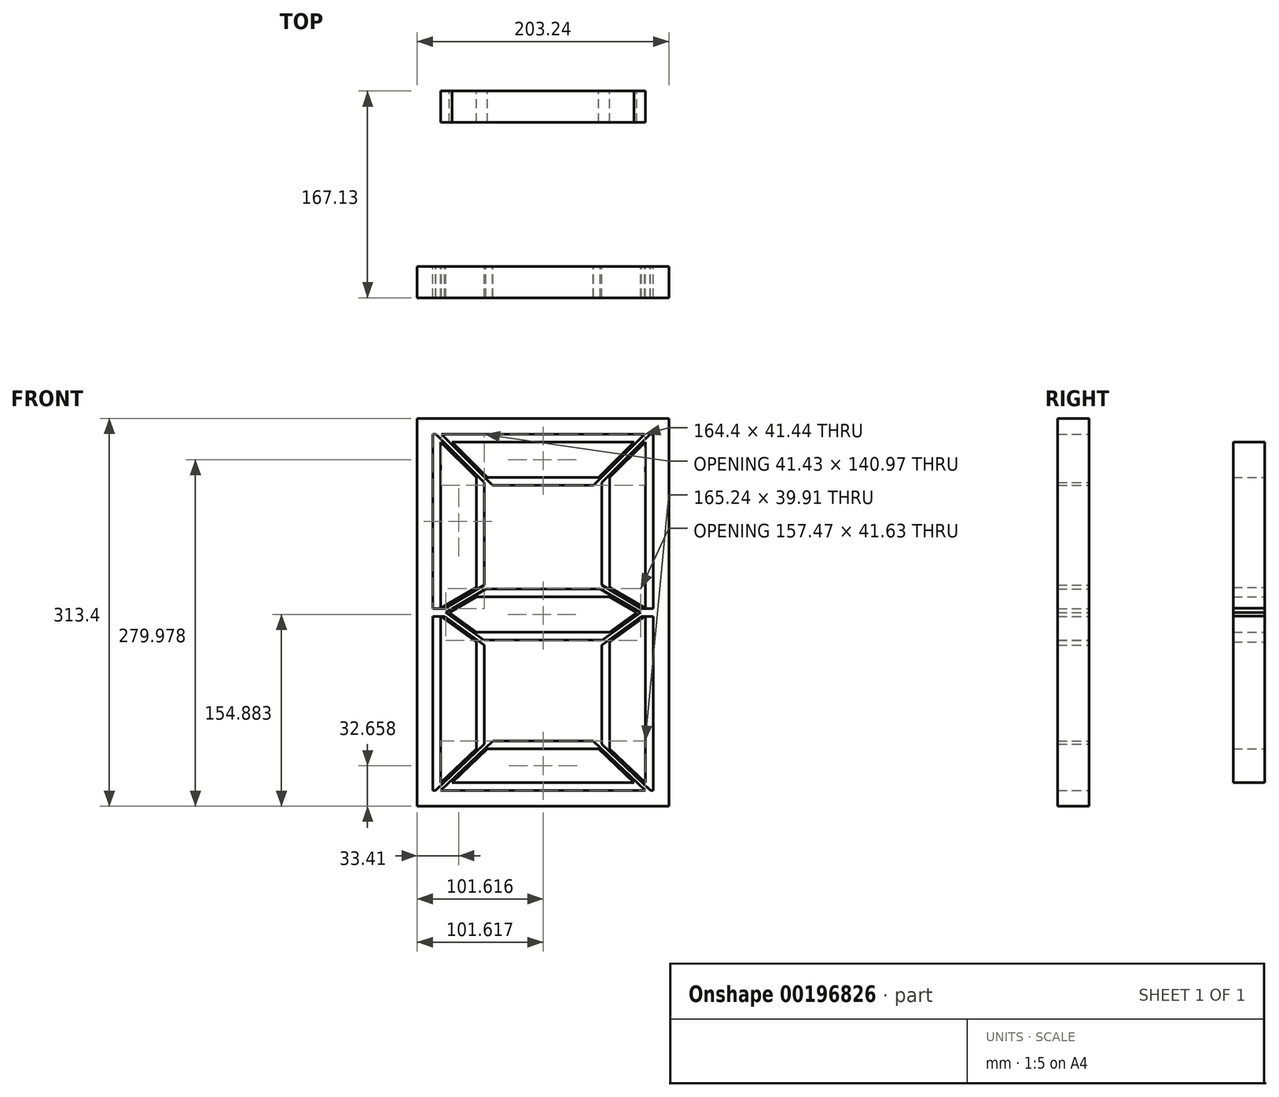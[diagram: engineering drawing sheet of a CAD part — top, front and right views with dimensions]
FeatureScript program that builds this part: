
annotation { "Feature Type Name" : "Feature", "Feature Type Description" : "" }
export const myFeature = defineFeature(function(context is Context, id is Id, definition is map)
    precondition{}
    {
        {
            var Q0;
            Q0=qCreatedBy(makeId("Front.planeOp"),FACE);
            var sketch = newSketch(context, id + "F0", { "sketchPlane" : qUnion([Q0])});
            skLineSegment(sketch, "E0.left", {"start": v(13.55, -44.45) * mm, "end": v(13.55, 44.45) * mm});
            skLineSegment(sketch, "E1", {"start": v(22.53, 44.45) * mm, "end": v(112.25, 44.45) * mm});
            skLineSegment(sketch, "E2", {"start": v(121.23, -44.45) * mm, "end": v(121.23, 44.45) * mm});
            skLineSegment(sketch, "E3.bottom", {"start": v(-27.88, 85.89) * mm, "end": v(161.85, 85.89) * mm});
            skLineSegment(sketch, "E3.top", {"start": v(-27.88, -214.8) * mm, "end": v(161.85, -214.8) * mm});
            skLineSegment(sketch, "E3.left", {"start": v(-27.88, 85.89) * mm, "end": v(-27.88, -214.8) * mm});
            skLineSegment(sketch, "E3.right", {"start": v(161.85, 85.89) * mm, "end": v(161.85, -214.8) * mm});
            skLineSegment(sketch, "E4", {"start": v(149.97, 73.19) * mm, "end": v(121.23, 44.45) * mm});
            skLineSegment(sketch, "E5", {"start": v(112.25, 44.45) * mm, "end": v(140.99, 73.19) * mm});
            skLineSegment(sketch, "E6", {"start": v(121.23, -174.9) * mm, "end": v(149.97, -202.1) * mm});
            skLineSegment(sketch, "E7", {"start": v(121.23, -88.37) * mm, "end": v(121.23, -174.9) * mm});
            skLineSegment(sketch, "E8", {"start": v(121.23, -88.37) * mm, "end": v(149.97, -67.64) * mm});
            skLineSegment(sketch, "E9", {"start": v(149.97, -61.3) * mm, "end": v(121.23, -44.45) * mm});
            skLineSegment(sketch, "E10", {"start": v(149.97, 73.19) * mm, "end": v(149.97, -61.3) * mm});
            skLineSegment(sketch, "E11", {"start": v(149.97, -202.1) * mm, "end": v(149.97, -67.64) * mm});
            skLineSegment(sketch, "E12", {"start": v(121.23, -51.81) * mm, "end": v(143.2, -64.69) * mm});
            skLineSegment(sketch, "E13", {"start": v(121.23, -80.54) * mm, "end": v(143.2, -64.69) * mm});
            skLineSegment(sketch, "E14", {"start": v(-15.17, -61.3) * mm, "end": v(-15.17, 73.19) * mm});
            skLineSegment(sketch, "E15", {"start": v(-15.17, -61.3) * mm, "end": v(13.55, -44.45) * mm});
            skLineSegment(sketch, "E16", {"start": v(121.23, -51.81) * mm, "end": v(13.55, -51.81) * mm});
            skLineSegment(sketch, "E17", {"start": v(13.55, -51.81) * mm, "end": v(-8.41, -64.69) * mm});
            skLineSegment(sketch, "E18", {"start": v(121.23, -80.54) * mm, "end": v(13.55, -80.54) * mm});
            skLineSegment(sketch, "E19", {"start": v(-8.41, -64.69) * mm, "end": v(13.55, -80.54) * mm});
            skLineSegment(sketch, "E20", {"start": v(-15.17, -67.64) * mm, "end": v(-15.17, -202.1) * mm});
            skLineSegment(sketch, "E21", {"start": v(-15.17, -67.64) * mm, "end": v(13.55, -88.37) * mm});
            skLineSegment(sketch, "E22", {"start": v(13.55, -88.37) * mm, "end": v(13.55, -174.9) * mm});
            skLineSegment(sketch, "E23", {"start": v(13.55, -174.9) * mm, "end": v(-15.17, -202.1) * mm});
            skLineSegment(sketch, "E24", {"start": v(140.99, 73.19) * mm, "end": v(-6.2, 73.19) * mm});
            skLineSegment(sketch, "E25", {"start": v(13.55, 44.45) * mm, "end": v(-15.17, 73.19) * mm});
            skLineSegment(sketch, "E26", {"start": v(22.53, 44.45) * mm, "end": v(-6.2, 73.19) * mm});
            skLineSegment(sketch, "E27", {"start": v(22.53, -174.9) * mm, "end": v(112.25, -174.9) * mm});
            skLineSegment(sketch, "E28", {"start": v(22.53, -174.9) * mm, "end": v(-6.2, -202.1) * mm});
            skLineSegment(sketch, "E29", {"start": v(-6.2, -202.1) * mm, "end": v(140.99, -202.1) * mm});
            skLineSegment(sketch, "E30", {"start": v(112.25, -174.9) * mm, "end": v(140.99, -202.1) * mm});
            skLineSegment(sketch, "E31", {"start": v(-15.17, 73.19) * mm, "end": v(-6.2, 73.19) * mm});
            skLineSegment(sketch, "E32", {"start": v(140.99, 73.19) * mm, "end": v(149.97, 73.19) * mm});
            skLineSegment(sketch, "E33", {"start": v(149.97, -202.1) * mm, "end": v(140.99, -202.1) * mm});
            skLineSegment(sketch, "E34", {"start": v(-6.2, -202.1) * mm, "end": v(-15.17, -202.1) * mm});
            skLineSegment(sketch, "E35", {"start": v(-15.17, -67.64) * mm, "end": v(-15.17, -61.3) * mm});
            skLineSegment(sketch, "E36", {"start": v(-8.41, -64.69) * mm, "end": v(-15.39, -64.69) * mm});
            skLineSegment(sketch, "E37", {"start": v(149.97, -61.3) * mm, "end": v(149.97, -67.64) * mm});
            skLineSegment(sketch, "E38", {"start": v(143.2, -64.69) * mm, "end": v(149.97, -64.69) * mm});
            skPoint(sketch, "E38.endSnap0", {"position": v(149.97, -64.47) * mm});
            skLineSegment(sketch, "E39", {"start": v(13.55, -51.81) * mm, "end": v(13.55, -51.81) * mm});
            skSolve(sketch);
        }
        {
            var Q0;
            Q0=makeQuery(id+"F0.imprint","IMPRINT",FACE,{"disambiguationData":[TD([[makeQuery(id+"F0.imprint","IMPRINT",EDGE,{"derivedFrom":sQuery(id+"F0.wireOp",EDGE,"E0.left")}),1.0]])]});
            var Q1;
            Q1=makeQuery(id+"F0.imprint","IMPRINT",FACE,{"disambiguationData":[TD([[makeQuery(id+"F0.imprint","IMPRINT",EDGE,{"derivedFrom":sQuery(id+"F0.wireOp",EDGE,"E1")}),1.0]])]});
            var Q2;
            Q2=makeQuery(id+"F0.imprint","IMPRINT",FACE,{"disambiguationData":[TD([[makeQuery(id+"F0.imprint","IMPRINT",EDGE,{"derivedFrom":sQuery(id+"F0.wireOp",EDGE,"E2")}),-1.0]])]});
            var Q3;
            Q3=makeQuery(id+"F0.imprint","IMPRINT",FACE,{"disambiguationData":[TD([[makeQuery(id+"F0.imprint","IMPRINT",EDGE,{"derivedFrom":sQuery(id+"F0.wireOp",EDGE,"E6")}),1.0]])]});
            var Q4;
            Q4=makeQuery(id+"F0.imprint","IMPRINT",FACE,{"disambiguationData":[TD([[makeQuery(id+"F0.imprint","IMPRINT",EDGE,{"derivedFrom":sQuery(id+"F0.wireOp",EDGE,"E20")}),1.0]])]});
            var Q5;
            Q5=makeQuery(id+"F0.imprint","IMPRINT",FACE,{"disambiguationData":[TD([[makeQuery(id+"F0.imprint","IMPRINT",EDGE,{"derivedFrom":sQuery(id+"F0.wireOp",EDGE,"E27")}),-1.0]])]});
            var Q6;
            Q6=makeQuery(id+"F0.imprint","IMPRINT",FACE,{"disambiguationData":[TD([[makeQuery(id+"F0.imprint","IMPRINT",EDGE,{"derivedFrom":sQuery(id+"F0.wireOp",EDGE,"E12")}),-1.0]])]});
            extrude(context, id + "F1", {"entities" : qUnion([Q0, Q1, Q2, Q3, Q4, Q5, Q6]), "depth" : 25.4 * mm, "offsetDistance" : 25.4 * mm});
        }
        {
            var Q0;
            Q0=makeQuery(id+"F1.opExtrude","CAP_FACE",FACE,{"disambiguationData":[OSD([sQuery(id+"F0.wireOp",EDGE,"E0.left"),sQuery(id+"F0.wireOp",EDGE,"E1"),sQuery(id+"F0.wireOp",EDGE,"E2"),sQuery(id+"F0.wireOp",EDGE,"E3.bottom"),sQuery(id+"F0.wireOp",EDGE,"E3.top"),sQuery(id+"F0.wireOp",EDGE,"E3.left"),sQuery(id+"F0.wireOp",EDGE,"E3.right"),sQuery(id+"F0.wireOp",EDGE,"E4"),sQuery(id+"F0.wireOp",EDGE,"E5"),sQuery(id+"F0.wireOp",EDGE,"E6"),sQuery(id+"F0.wireOp",EDGE,"E7"),sQuery(id+"F0.wireOp",EDGE,"E8"),sQuery(id+"F0.wireOp",EDGE,"E9"),sQuery(id+"F0.wireOp",EDGE,"E10"),sQuery(id+"F0.wireOp",EDGE,"E11"),sQuery(id+"F0.wireOp",EDGE,"E12"),sQuery(id+"F0.wireOp",EDGE,"E13"),sQuery(id+"F0.wireOp",EDGE,"E14"),sQuery(id+"F0.wireOp",EDGE,"E15"),sQuery(id+"F0.wireOp",EDGE,"E16"),sQuery(id+"F0.wireOp",EDGE,"E17"),sQuery(id+"F0.wireOp",EDGE,"E18"),sQuery(id+"F0.wireOp",EDGE,"E19"),sQuery(id+"F0.wireOp",EDGE,"E20"),sQuery(id+"F0.wireOp",EDGE,"E21"),sQuery(id+"F0.wireOp",EDGE,"E22"),sQuery(id+"F0.wireOp",EDGE,"E23"),sQuery(id+"F0.wireOp",EDGE,"E24"),sQuery(id+"F0.wireOp",EDGE,"E25"),sQuery(id+"F0.wireOp",EDGE,"E26"),sQuery(id+"F0.wireOp",EDGE,"E27"),sQuery(id+"F0.wireOp",EDGE,"E28"),sQuery(id+"F0.wireOp",EDGE,"E29"),sQuery(id+"F0.wireOp",EDGE,"E30")])],"isStart":false});
            cPlane(context, id + "F2", {"entities" : qUnion([Q0]), "cplaneType" : CPlaneType.OFFSET, "offset" : 116.33 * mm, "width" : 152.4 * mm, "height" : 152.4 * mm});
        }
        {
            var Q0;
            Q0=qCreatedBy(id+"F2.planeOp",FACE);
            var sketch = newSketch(context, id + "F3", { "sketchPlane" : qUnion([Q0])});
            skLineSegment(sketch, "E40.left", {"start": v(19.9, 38.1) * mm, "end": v(19.9, -42.58) * mm});
            skLineSegment(sketch, "E40.right", {"start": v(114.88, 38.1) * mm, "end": v(114.88, -42.58) * mm});
            skLineSegment(sketch, "E41.bottom", {"start": v(-21.52, 79.54) * mm, "end": v(156.32, 79.54) * mm});
            skLineSegment(sketch, "E41.top", {"start": v(-21.52, -208.46) * mm, "end": v(156.32, -208.46) * mm});
            skLineSegment(sketch, "E41.left", {"start": v(-21.52, 79.54) * mm, "end": v(-21.52, -208.46) * mm});
            skLineSegment(sketch, "E41.right", {"start": v(156.32, 79.54) * mm, "end": v(156.32, -208.46) * mm});
            skLineSegment(sketch, "E42.bottom", {"start": v(21.22, -45.46) * mm, "end": v(113.56, -45.46) * mm});
            skLineSegment(sketch, "E42.top", {"start": v(19.9, -86.89) * mm, "end": v(114.88, -86.89) * mm});
            skLineSegment(sketch, "E43.trimOffspring", {"start": v(114.88, -86.89) * mm, "end": v(114.88, -87.1) * mm});
            skLineSegment(sketch, "E44.trimOffspring", {"start": v(19.9, -86.89) * mm, "end": v(19.9, -87.1) * mm});
            skLineSegment(sketch, "E45", {"start": v(-14.8, 79.54) * mm, "end": v(26.62, 38.1) * mm});
            skLineSegment(sketch, "E46", {"start": v(19.9, 40.36) * mm, "end": v(-19.26, 79.54) * mm});
            skLineSegment(sketch, "E47", {"start": v(149.6, 79.54) * mm, "end": v(108.16, 38.1) * mm});
            skLineSegment(sketch, "E48", {"start": v(114.88, 40.36) * mm, "end": v(154.05, 79.54) * mm});
            skLineSegment(sketch, "E49.trimOffspring", {"start": v(26.62, 38.1) * mm, "end": v(108.16, 38.1) * mm});
            skLineSegment(sketch, "E50", {"start": v(154.34, -208.46) * mm, "end": v(114.88, -171.09) * mm});
            skLineSegment(sketch, "E51", {"start": v(107.87, -168.55) * mm, "end": v(150.02, -208.46) * mm});
            skLineSegment(sketch, "E52", {"start": v(19.9, -171.08) * mm, "end": v(-19.55, -208.46) * mm});
            skLineSegment(sketch, "E53", {"start": v(-15.23, -208.46) * mm, "end": v(26.9, -168.55) * mm});
            skLineSegment(sketch, "E54.trimOffspring", {"start": v(26.9, -168.55) * mm, "end": v(107.87, -168.55) * mm});
            skLineSegment(sketch, "E55", {"start": v(146.13, -64.55) * mm, "end": v(114.88, -87.1) * mm});
            skLineSegment(sketch, "E56", {"start": v(114.88, -90.97) * mm, "end": v(147.04, -67.78) * mm});
            skLineSegment(sketch, "E57", {"start": v(114.88, -42.58) * mm, "end": v(147.04, -61.43) * mm});
            skLineSegment(sketch, "E58", {"start": v(146.13, -64.55) * mm, "end": v(113.56, -45.46) * mm});
            skLineSegment(sketch, "E59", {"start": v(19.9, -90.98) * mm, "end": v(-12.25, -67.78) * mm});
            skLineSegment(sketch, "E60", {"start": v(-11.34, -64.55) * mm, "end": v(19.9, -87.1) * mm});
            skLineSegment(sketch, "E61.trimOffspring", {"start": v(19.9, -90.98) * mm, "end": v(19.9, -168.55) * mm});
            skLineSegment(sketch, "E62", {"start": v(-11.34, -64.55) * mm, "end": v(21.22, -45.46) * mm});
            skPoint(sketch, "E63.orphan", {"position": v(114.88, -45.46) * mm});
            skLineSegment(sketch, "E64.trimOffspring", {"start": v(114.88, -90.97) * mm, "end": v(114.88, -168.55) * mm});
            skLineSegment(sketch, "E65", {"start": v(147.04, -61.43) * mm, "end": v(156.32, -61.43) * mm});
            skLineSegment(sketch, "E66", {"start": v(147.04, -67.78) * mm, "end": v(156.32, -67.78) * mm});
            skLineSegment(sketch, "E67", {"start": v(-12.25, -61.43) * mm, "end": v(-21.52, -61.43) * mm});
            skLineSegment(sketch, "E68", {"start": v(-12.25, -67.78) * mm, "end": v(-21.52, -67.78) * mm});
            skLineSegment(sketch, "E69", {"start": v(-12.25, -61.43) * mm, "end": v(19.9, -42.58) * mm});
            skLineSegment(sketch, "E70.bottom", {"start": v(-34.22, 92.24) * mm, "end": v(169.02, 92.24) * mm});
            skLineSegment(sketch, "E70.top", {"start": v(-34.22, -221.16) * mm, "end": v(169.02, -221.16) * mm});
            skLineSegment(sketch, "E70.left", {"start": v(-34.22, 92.24) * mm, "end": v(-34.22, -221.16) * mm});
            skLineSegment(sketch, "E70.right", {"start": v(169.02, 92.24) * mm, "end": v(169.02, -221.16) * mm});
            skLineSegment(sketch, "E71", {"start": v(19.9, 38.1) * mm, "end": v(19.9, 40.36) * mm});
            skLineSegment(sketch, "E72", {"start": v(114.88, 38.1) * mm, "end": v(114.88, 40.36) * mm});
            skLineSegment(sketch, "E73", {"start": v(114.88, -168.55) * mm, "end": v(114.88, -171.09) * mm});
            skLineSegment(sketch, "E74", {"start": v(19.9, -168.55) * mm, "end": v(19.9, -171.08) * mm});
            skSolve(sketch);
        }
        {
            var Q0;
            Q0 = qSketchRegion(id + "F3", true);
            var Q1;
            Q1=makeQuery(id+"F3.imprint","IMPRINT",FACE,{"disambiguationData":[TD([[makeQuery(id+"F3.imprint","IMPRINT",EDGE,{"derivedFrom":sQuery(id+"F3.wireOp",EDGE,"E40.bottom")}),-1.0]])]});
            var Q2;
            Q2=makeQuery(id+"F3.imprint","IMPRINT",FACE,{"disambiguationData":[TD([[makeQuery(id+"F3.imprint","IMPRINT",EDGE,{"derivedFrom":sQuery(id+"F3.wireOp",EDGE,"E40.left")}),1.0]])]});
            extrude(context, id + "F4", {"entities" : qUnion([Q0, Q1, Q2]), "depth" : 25.4 * mm, "offsetDistance" : 25.4 * mm});
        }
    });
